# Revit family: BEG-97001
name_source: partatom
category: Dispositifs d'éclairage
revit_build: Autodesk Revit 2015 (Build: 20140606_1530(x64)
units: mm (PartAtom-declared; Revit-internal decimal feet)

## types (1)
- BEG-97001
    Ambiant temperature = -25°C to +50°C
    Brand = LUXOMAT
    Class = 2
    Code d'assemblage = D5010200
    Commentaires du type = RC-plus next, 130°, white
    Consumption = 0.51W
    Elévation par défaut = 250 cm
    Fabricant = B.E.G
    IP = 54
    Image du type = 97001.jpg
    Installation height max = 400 cm
    Installation type = Wall or ceiling monting
    Modèle = RC-plus next, 130°, white
    Mounting height max = 400 cm
    Power voltage = 110-240 V AC
    Ref = 97001
    Relay = 16A
    Switching power Cos ɸ =0,5 = 1500W
    Switching power Cos ɸ =1 = 3000W
    Switching power LED = 300W
    Type of output = SWITCH
    URL = http://www.luxomat.com

## geometry (parser evidence)
native form markers: Extrusion x2
no freeform markers — native parametric forms only
